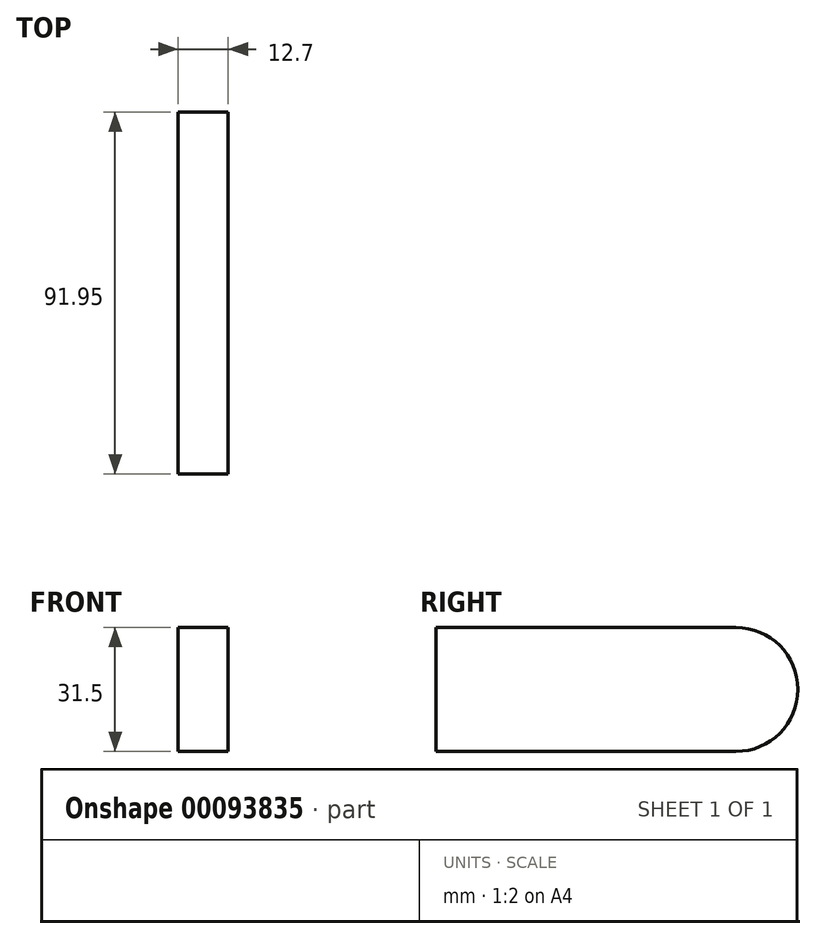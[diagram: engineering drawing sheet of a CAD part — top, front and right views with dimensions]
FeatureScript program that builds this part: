
annotation { "Feature Type Name" : "Feature", "Feature Type Description" : "" }
export const myFeature = defineFeature(function(context is Context, id is Id, definition is map)
    precondition{}
    {
        {
            var Q0;
            Q0=qCreatedBy(makeId("Right.planeOp"),FACE);
            var sketch = newSketch(context, id + "F0", { "sketchPlane" : qUnion([Q0])});
            skLineSegment(sketch, "E0.bottom", {"start": v(-57.17, 62.37) * mm, "end": v(19.03, 62.37) * mm});
            skLineSegment(sketch, "E0.top", {"start": v(-57.17, 30.87) * mm, "end": v(19.03, 30.87) * mm});
            skLineSegment(sketch, "E0.left", {"start": v(-57.17, 62.37) * mm, "end": v(-57.17, 30.87) * mm});
            skLineSegment(sketch, "E0.right", {"start": v(19.03, 62.37) * mm, "end": v(19.03, 30.87) * mm});
            skArc(sketch, "E1", {"start": v(19.03, 30.87) * mm, "mid": v(34.78, 46.62) * mm, "end": v(19.03, 62.37) * mm});
            skSolve(sketch);
        }
        {
            var Q0;
            Q0 = qSketchRegion(id + "F0", true);
            extrude(context, id + "F1", {"entities" : qUnion([Q0]), "depth" : 12.7 * mm});
        }
    });
